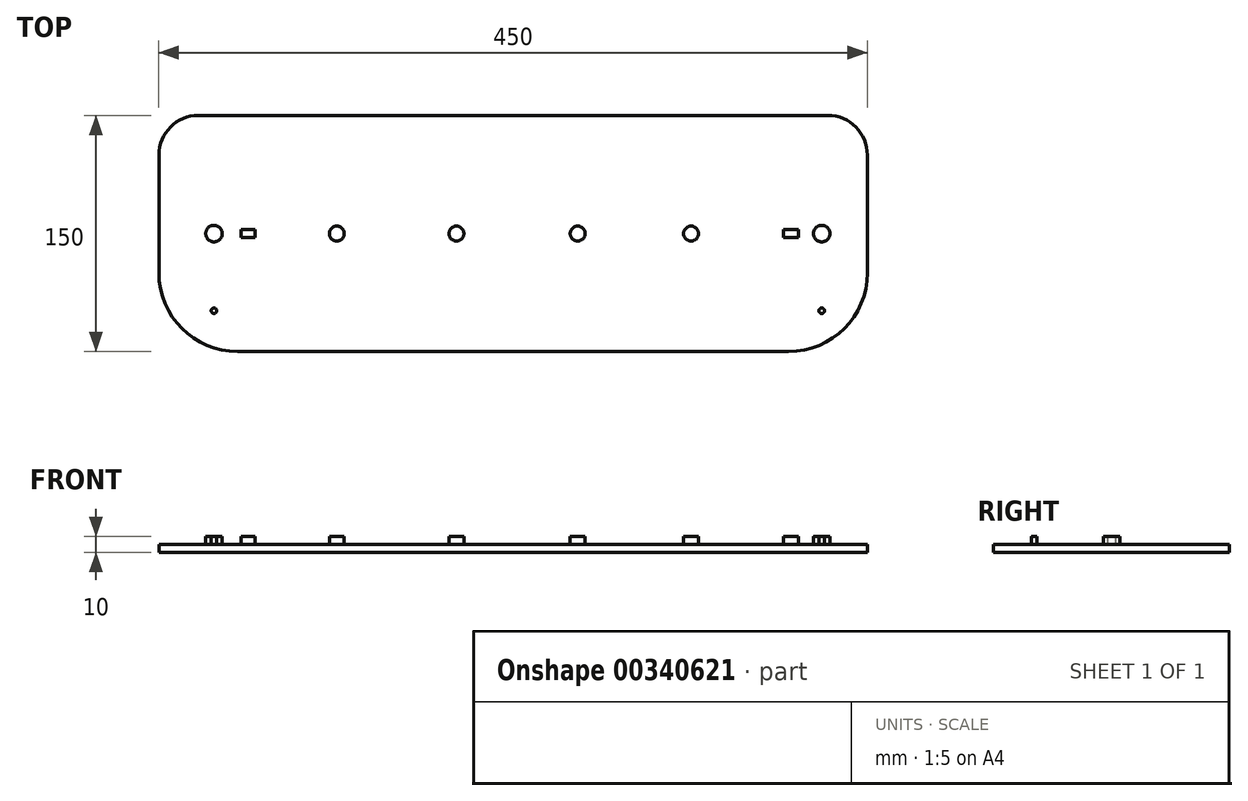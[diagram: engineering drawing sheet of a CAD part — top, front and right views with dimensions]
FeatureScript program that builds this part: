
annotation { "Feature Type Name" : "Feature", "Feature Type Description" : "" }
export const myFeature = defineFeature(function(context is Context, id is Id, definition is map)
    precondition{}
    {
        {
            var Q0;
            Q0=qCreatedBy(makeId("Top.planeOp"),FACE);
            var sketch = newSketch(context, id + "F0", { "sketchPlane" : qUnion([Q0])});
            skLineSegment(sketch, "E0.bottom", {"start": v(-388.94, 124.38) * mm, "end": v(61.06, 124.38) * mm});
            skLineSegment(sketch, "E0.top", {"start": v(-388.94, -25.62) * mm, "end": v(61.06, -25.62) * mm});
            skLineSegment(sketch, "E0.left", {"start": v(-388.94, 124.38) * mm, "end": v(-388.94, -25.62) * mm});
            skLineSegment(sketch, "E0.right", {"start": v(61.06, 124.38) * mm, "end": v(61.06, -25.62) * mm});
            skSolve(sketch);
        }
        {
            var Q0;
            Q0=makeQuery(id+"F0.imprint","IMPRINT",FACE,{"disambiguationData":[TD([[makeQuery(id+"F0.imprint","IMPRINT",EDGE,{"derivedFrom":sQuery(id+"F0.wireOp",EDGE,"E0.bottom")}),-1.0]])]});
            extrude(context, id + "F1", {"entities" : qUnion([Q0]), "depth" : 5 * mm});
        }
        {
            var Q0;
            Q0=makeQuery(id+"F1.opExtrude","CAP_FACE",FACE,{"disambiguationData":[OSD([sQuery(id+"F0.wireOp",EDGE,"E0.bottom"),sQuery(id+"F0.wireOp",EDGE,"E0.top"),sQuery(id+"F0.wireOp",EDGE,"E0.left"),sQuery(id+"F0.wireOp",EDGE,"E0.right")])],"isStart":false});
            var sketch = newSketch(context, id + "F2", { "sketchPlane" : qUnion([Q0])});
            skPoint(sketch, "E1", {"position": v(-388.94, 49.38) * mm});
            skPoint(sketch, "E2", {"position": v(-163.94, 49.38) * mm});
            skPoint(sketch, "E2.positionSnap0", {"position": v(-163.94, -25.62) * mm});
            skPoint(sketch, "E3", {"position": v(61.06, 49.38) * mm});
            skLineSegment(sketch, "E4", {"start": v(-388.94, 49.38) * mm, "end": v(61.06, 49.38) * mm, "construction": true});
            skPoint(sketch, "E5", {"position": v(-353.94, 49.38) * mm});
            skPoint(sketch, "E6", {"position": v(-275.94, 49.38) * mm});
            skPoint(sketch, "E7", {"position": v(-199.94, 49.38) * mm});
            skPoint(sketch, "E8", {"position": v(-122.94, 49.38) * mm});
            skPoint(sketch, "E9", {"position": v(-50.94, 49.38) * mm});
            skPoint(sketch, "E10", {"position": v(32.06, 49.38) * mm});
            skPoint(sketch, "E11", {"position": v(-332.19, 49.38) * mm});
            skPoint(sketch, "E12", {"position": v(-232, 49.38) * mm});
            skPoint(sketch, "E13", {"position": v(-85.98, 49.38) * mm});
            skPoint(sketch, "E14", {"position": v(12.56, 49.38) * mm});
            skLineSegment(sketch, "E15.bottom", {"start": v(-336.69, 51.88) * mm, "end": v(-327.69, 51.88) * mm});
            skLineSegment(sketch, "E15.top", {"start": v(-336.69, 46.88) * mm, "end": v(-327.69, 46.88) * mm});
            skLineSegment(sketch, "E15.left", {"start": v(-336.69, 51.88) * mm, "end": v(-336.69, 46.88) * mm});
            skLineSegment(sketch, "E15.right", {"start": v(-327.69, 51.88) * mm, "end": v(-327.69, 46.88) * mm});
            skCircle(sketch, "E16", {"center": v(-353.94, 49.38) * mm, "radius": 5.25 * mm});
            skCircle(sketch, "E17", {"center": v(-275.94, 49.38) * mm, "radius": 4.75 * mm});
            skCircle(sketch, "E18", {"center": v(-199.94, 49.38) * mm, "radius": 4.75 * mm});
            skCircle(sketch, "E19", {"center": v(-122.94, 49.38) * mm, "radius": 4.75 * mm});
            skCircle(sketch, "E20", {"center": v(-50.94, 49.38) * mm, "radius": 4.75 * mm});
            skCircle(sketch, "E21", {"center": v(32.06, 49.38) * mm, "radius": 5.25 * mm});
            skLineSegment(sketch, "E22.bottom", {"start": v(7.81, 51.88) * mm, "end": v(17.31, 51.88) * mm});
            skLineSegment(sketch, "E22.top", {"start": v(7.81, 46.88) * mm, "end": v(17.31, 46.88) * mm});
            skLineSegment(sketch, "E22.left", {"start": v(7.81, 51.88) * mm, "end": v(7.81, 46.88) * mm});
            skLineSegment(sketch, "E22.right", {"start": v(17.31, 51.88) * mm, "end": v(17.31, 46.88) * mm});
            skPoint(sketch, "E23", {"position": v(-353.94, 0.38) * mm});
            skCircle(sketch, "E24", {"center": v(-353.94, 0.38) * mm, "radius": 1.75 * mm});
            skPoint(sketch, "E25", {"position": v(32.06, 0.38) * mm});
            skCircle(sketch, "E26", {"center": v(32.06, 0.38) * mm, "radius": 1.75 * mm});
            skSolve(sketch);
        }
        {
            var Q0;
            Q0 = qSketchRegion(id + "F2", true);
            extrude(context, id + "F3", {"entities" : qUnion([Q0]), "operationType" : NewBodyOperationType.ADD, "depth" : 5 * mm});
        }
        {
            var Q0;
            Q0=makeQuery(id+"F1.opExtrude","SWEPT_EDGE",EDGE,{"disambiguationData":[OSD([sQuery(id+"F0.wireOp",EDGE,"E0.bottom"),sQuery(id+"F0.wireOp",EDGE,"E0.left")])]});
            var Q1;
            Q1=makeQuery(id+"F1.opExtrude","SWEPT_EDGE",EDGE,{"disambiguationData":[OSD([sQuery(id+"F0.wireOp",EDGE,"E0.bottom"),sQuery(id+"F0.wireOp",EDGE,"E0.right")])]});
            fillet(context, id + "F4", {"entities" : qUnion([Q0, Q1]), "radius" : 25 * mm, "tangentPropagation" : true, "allowEdgeOverflow" : false});
        }
        {
            var Q0;
            Q0=makeQuery(id+"F1.opExtrude","SWEPT_EDGE",EDGE,{"disambiguationData":[OSD([sQuery(id+"F0.wireOp",EDGE,"E0.top"),sQuery(id+"F0.wireOp",EDGE,"E0.left")])]});
            var Q1;
            Q1=makeQuery(id+"F1.opExtrude","SWEPT_EDGE",EDGE,{"disambiguationData":[OSD([sQuery(id+"F0.wireOp",EDGE,"E0.top"),sQuery(id+"F0.wireOp",EDGE,"E0.right")])]});
            fillet(context, id + "F5", {"entities" : qUnion([Q0, Q1]), "radius" : 50 * mm, "tangentPropagation" : true, "allowEdgeOverflow" : false});
        }
    });
